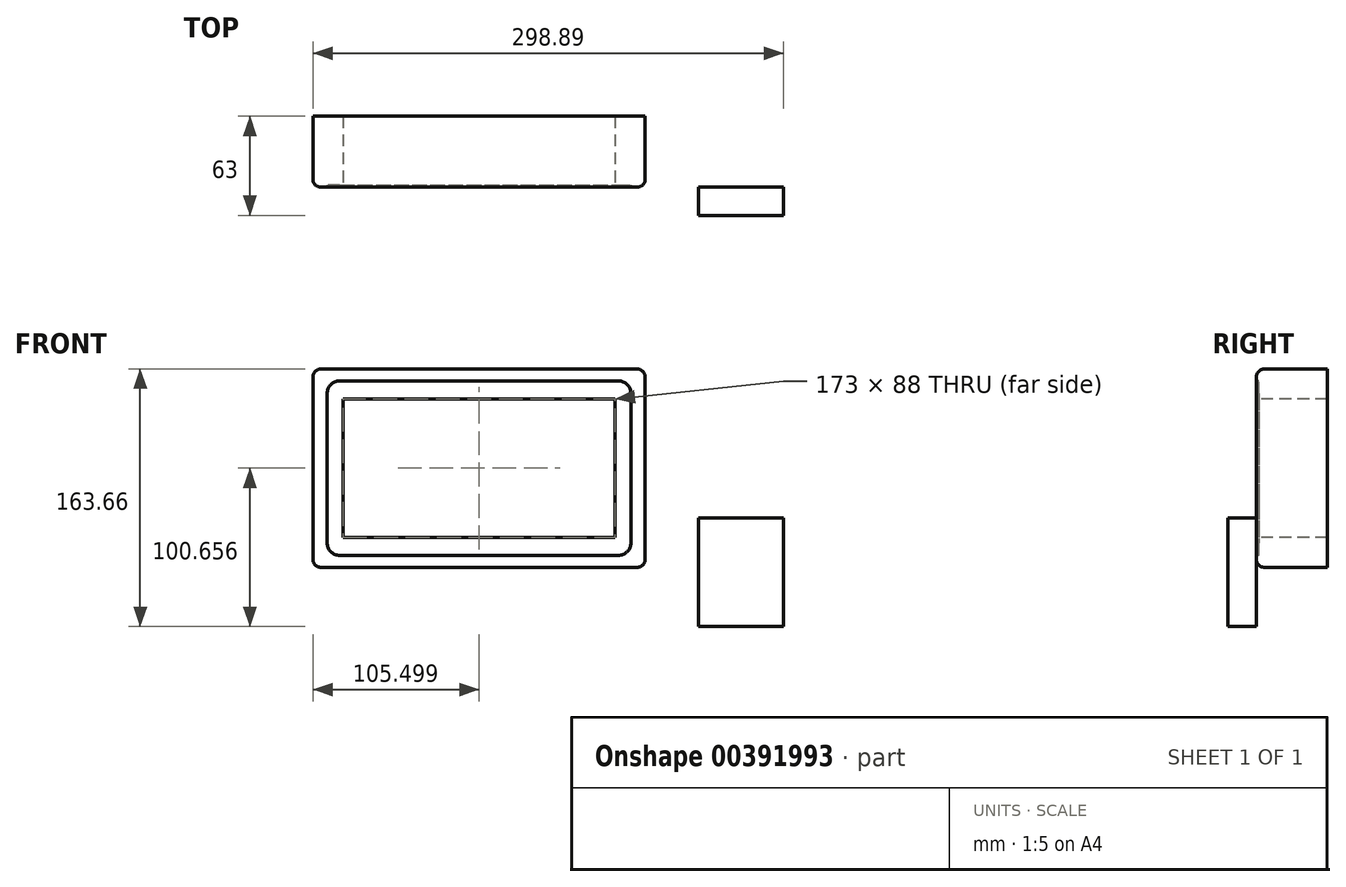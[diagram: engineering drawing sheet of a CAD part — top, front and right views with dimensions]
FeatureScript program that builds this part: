
annotation { "Feature Type Name" : "Feature", "Feature Type Description" : "" }
export const myFeature = defineFeature(function(context is Context, id is Id, definition is map)
    precondition{}
    {
        {
            var Q0;
            Q0=qCreatedBy(makeId("Front.planeOp"),FACE);
            var sketch = newSketch(context, id + "F0", { "sketchPlane" : qUnion([Q0])});
            skLineSegment(sketch, "E0.bottom", {"start": v(-54.78, 100.65) * mm, "end": v(156.22, 100.65) * mm});
            skLineSegment(sketch, "E0.top", {"start": v(-54.78, -25.35) * mm, "end": v(156.22, -25.35) * mm});
            skLineSegment(sketch, "E0.left", {"start": v(-54.78, 100.65) * mm, "end": v(-54.78, -25.35) * mm});
            skLineSegment(sketch, "E0.right", {"start": v(156.22, 100.65) * mm, "end": v(156.22, -25.35) * mm});
            skLineSegment(sketch, "E1.0", {"start": v(137.22, 81.65) * mm, "end": v(137.22, -6.35) * mm});
            skLineSegment(sketch, "E1.1", {"start": v(-35.78, 81.65) * mm, "end": v(137.22, 81.65) * mm});
            skLineSegment(sketch, "E1.2", {"start": v(-35.78, 81.65) * mm, "end": v(-35.78, -6.35) * mm});
            skLineSegment(sketch, "E1.3", {"start": v(-35.78, -6.35) * mm, "end": v(137.22, -6.35) * mm});
            skLineSegment(sketch, "E2.bottom", {"start": v(-37.76, 93.03) * mm, "end": v(139.2, 93.03) * mm});
            skLineSegment(sketch, "E2.top", {"start": v(-37.76, -17.73) * mm, "end": v(139.2, -17.73) * mm});
            skLineSegment(sketch, "E2.left", {"start": v(-45.76, 85.03) * mm, "end": v(-45.76, -9.73) * mm});
            skLineSegment(sketch, "E2.right", {"start": v(147.2, 85.03) * mm, "end": v(147.2, -9.73) * mm});
            skLineSegment(sketch, "E3", {"start": v(50.72, -25.35) * mm, "end": v(50.72, -17.73) * mm, "construction": true});
            skLineSegment(sketch, "E4", {"start": v(-54.78, 37.65) * mm, "end": v(-45.76, 37.65) * mm, "construction": true});
            skPoint(sketch, "E5.visualSharp", {"position": v(147.2, 93.03) * mm});
            skArc(sketch, "E5.filletArc", {"start": v(147.2, 85.03) * mm, "mid": v(144.86, 90.68) * mm, "end": v(139.2, 93.03) * mm});
            skPoint(sketch, "E6.visualSharp", {"position": v(147.2, -17.73) * mm});
            skArc(sketch, "E6.filletArc", {"start": v(139.2, -17.73) * mm, "mid": v(144.86, -15.4) * mm, "end": v(147.2, -9.73) * mm});
            skPoint(sketch, "E7.visualSharp", {"position": v(-45.76, -17.73) * mm});
            skArc(sketch, "E7.filletArc", {"start": v(-45.76, -9.73) * mm, "mid": v(-43.42, -15.4) * mm, "end": v(-37.76, -17.73) * mm});
            skPoint(sketch, "E8.visualSharp", {"position": v(-45.76, 93.03) * mm});
            skArc(sketch, "E8.filletArc", {"start": v(-37.76, 93.03) * mm, "mid": v(-43.42, 90.68) * mm, "end": v(-45.76, 85.03) * mm});
            skSolve(sketch);
        }
        {
            var Q0;
            Q0=makeQuery(id+"F0.imprint","IMPRINT",FACE,{"disambiguationData":[TD([[makeQuery(id+"F0.imprint","IMPRINT",EDGE,{"derivedFrom":sQuery(id+"F0.wireOp",EDGE,"E0.bottom")}),-1.0]])]});
            var Q1;
            Q1=makeQuery(id+"F0.imprint","IMPRINT",FACE,{"disambiguationData":[TD([[makeQuery(id+"F0.imprint","IMPRINT",EDGE,{"derivedFrom":sQuery(id+"F0.wireOp",EDGE,"E1.0")}),1.0]])]});
            extrude(context, id + "F1", {"entities" : qUnion([Q0, Q1]), "oppositeDirection" : true, "depth" : 45 * mm});
        }
        {
            var Q0;
            Q0=makeQuery(id+"F0.imprint","IMPRINT",FACE,{"disambiguationData":[TD([[makeQuery(id+"F0.imprint","IMPRINT",EDGE,{"derivedFrom":sQuery(id+"F0.wireOp",EDGE,"E1.0")}),1.0]])]});
            extrude(context, id + "F2", {"entities" : qUnion([Q0]), "operationType" : NewBodyOperationType.REMOVE, "oppositeDirection" : true, "depth" : 1.4 * mm});
        }
        {
            var Q0;
            Q0=makeQuery(id+"F1.opExtrude","CAP_EDGE",EDGE,{"disambiguationData":[OSD([sQuery(id+"F0.wireOp",EDGE,"E0.top")])],"isStart":true});
            var Q1;
            Q1=makeQuery(id+"F1.opExtrude","CAP_EDGE",EDGE,{"disambiguationData":[OSD([sQuery(id+"F0.wireOp",EDGE,"E0.right")])],"isStart":true});
            var Q2;
            Q2=makeQuery(id+"F1.opExtrude","SWEPT_EDGE",EDGE,{"disambiguationData":[OSD([sQuery(id+"F0.wireOp",EDGE,"E0.top"),sQuery(id+"F0.wireOp",EDGE,"E0.right")])]});
            var Q3;
            Q3=makeQuery(id+"F1.opExtrude","SWEPT_EDGE",EDGE,{"disambiguationData":[OSD([sQuery(id+"F0.wireOp",EDGE,"E0.top"),sQuery(id+"F0.wireOp",EDGE,"E0.left")])]});
            var Q4;
            Q4=makeQuery(id+"F1.opExtrude","CAP_EDGE",EDGE,{"disambiguationData":[OSD([sQuery(id+"F0.wireOp",EDGE,"E0.left")])],"isStart":true});
            var Q5;
            Q5=makeQuery(id+"F1.opExtrude","CAP_EDGE",EDGE,{"disambiguationData":[OSD([sQuery(id+"F0.wireOp",EDGE,"E0.bottom")])],"isStart":true});
            var Q6;
            Q6=makeQuery(id+"F1.opExtrude","SWEPT_EDGE",EDGE,{"disambiguationData":[OSD([sQuery(id+"F0.wireOp",EDGE,"E0.bottom"),sQuery(id+"F0.wireOp",EDGE,"E0.right")])]});
            var Q7;
            Q7=makeQuery(id+"F1.opExtrude","SWEPT_EDGE",EDGE,{"disambiguationData":[OSD([sQuery(id+"F0.wireOp",EDGE,"E0.bottom"),sQuery(id+"F0.wireOp",EDGE,"E0.left")])]});
            fillet(context, id + "F3", {"entities" : qUnion([Q0, Q1, Q2, Q3, Q4, Q5, Q6, Q7]), "radius" : 5 * mm, "tangentPropagation" : true, "allowEdgeOverflow" : false});
        }
        {
            var Q0;
            Q0=qCreatedBy(makeId("Front.planeOp"),FACE);
            var sketch = newSketch(context, id + "F4", { "sketchPlane" : qUnion([Q0])});
            skLineSegment(sketch, "E9.bottom", {"start": v(190.11, 6) * mm, "end": v(244.11, 6) * mm});
            skLineSegment(sketch, "E9.top", {"start": v(190.11, -63) * mm, "end": v(244.11, -63) * mm});
            skLineSegment(sketch, "E9.left", {"start": v(190.11, 6) * mm, "end": v(190.11, -63) * mm});
            skLineSegment(sketch, "E9.right", {"start": v(244.11, 6) * mm, "end": v(244.11, -63) * mm});
            skSolve(sketch);
        }
        {
            var Q0;
            Q0=makeQuery(id+"F4.imprint","IMPRINT",FACE,{"disambiguationData":[TD([[makeQuery(id+"F4.imprint","IMPRINT",EDGE,{"derivedFrom":sQuery(id+"F4.wireOp",EDGE,"E9.bottom")}),-1.0]])]});
            extrude(context, id + "F5", {"entities" : qUnion([Q0]), "depth" : 18 * mm});
        }
    });
